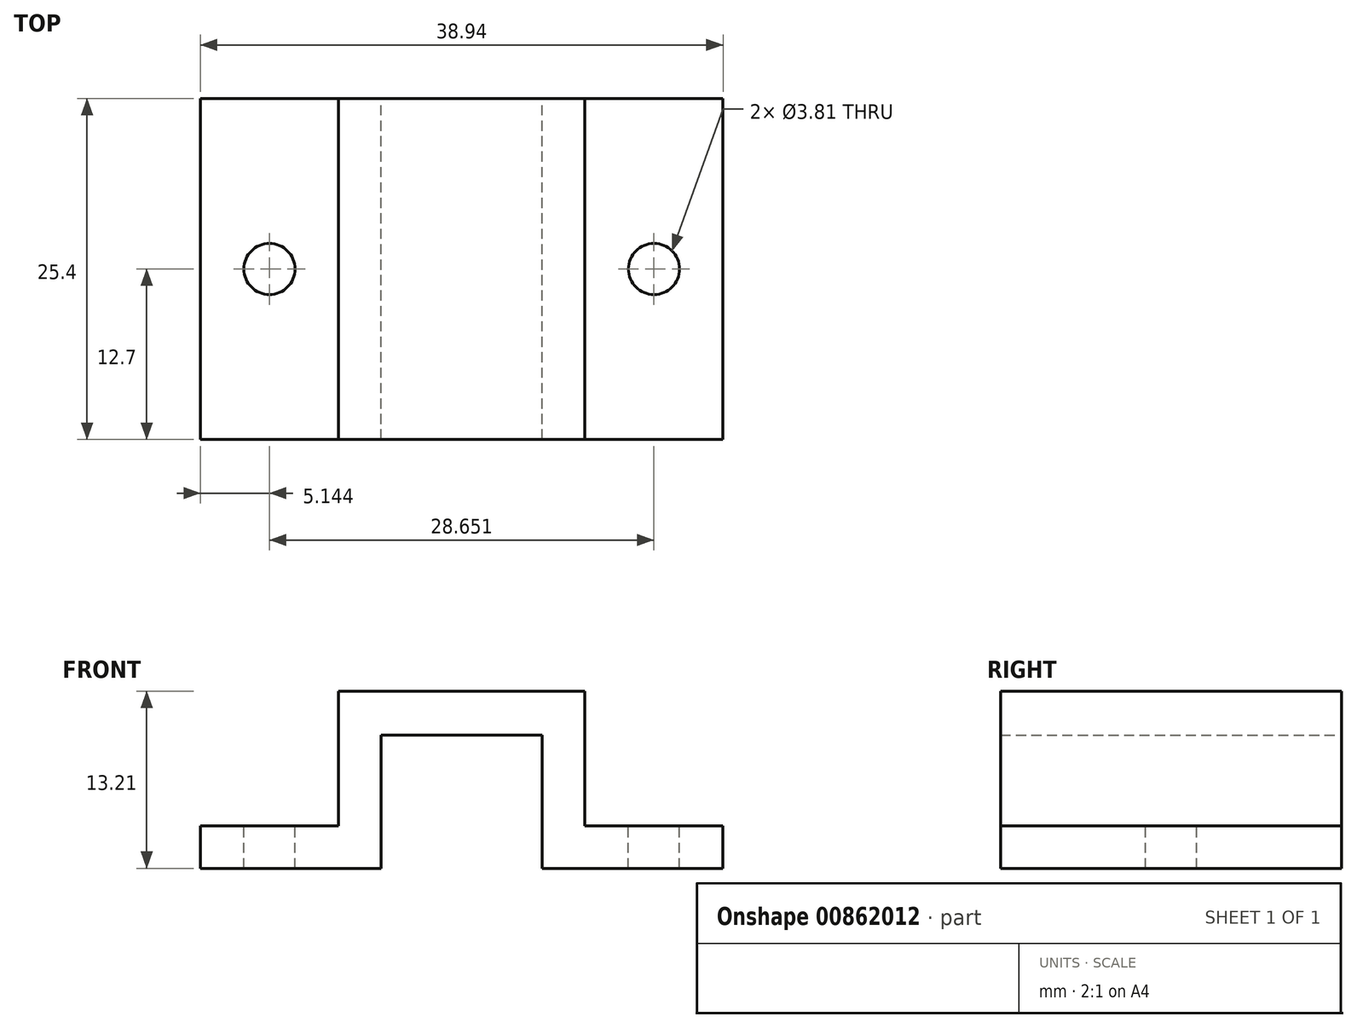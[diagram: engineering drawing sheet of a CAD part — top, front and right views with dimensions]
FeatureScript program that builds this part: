
annotation { "Feature Type Name" : "Feature", "Feature Type Description" : "" }
export const myFeature = defineFeature(function(context is Context, id is Id, definition is map)
    precondition{}
    {
        {
            var Q0;
            Q0=qCreatedBy(makeId("Front.planeOp"),FACE);
            var sketch = newSketch(context, id + "F0", { "sketchPlane" : qUnion([Q0])});
            skLineSegment(sketch, "E0", {"start": v(0, 0) * mm, "end": v(-6, 0) * mm});
            skLineSegment(sketch, "E1", {"start": v(-6, 0) * mm, "end": v(-6, -9.93) * mm});
            skLineSegment(sketch, "E2", {"start": v(-6, -9.93) * mm, "end": v(-19.47, -9.93) * mm});
            skLineSegment(sketch, "E3", {"start": v(-19.47, -9.93) * mm, "end": v(-19.47, -6.76) * mm});
            skLineSegment(sketch, "E4", {"start": v(-19.47, -6.76) * mm, "end": v(-9.18, -6.76) * mm});
            skLineSegment(sketch, "E5", {"start": v(-9.18, -6.76) * mm, "end": v(-9.18, 3.28) * mm});
            skLineSegment(sketch, "E6", {"start": v(-9.18, 3.28) * mm, "end": v(0, 3.28) * mm});
            skLineSegment(sketch, "E7.MirrorCS", {"start": v(6, 0) * mm, "end": v(6, -9.93) * mm});
            skLineSegment(sketch, "E8.MirrorCS", {"start": v(9.18, 3.28) * mm, "end": v(0, 3.28) * mm});
            skLineSegment(sketch, "E9.MirrorCS", {"start": v(9.18, -6.76) * mm, "end": v(9.18, 3.28) * mm});
            skLineSegment(sketch, "E10.MirrorCS", {"start": v(19.47, -9.93) * mm, "end": v(19.47, -6.76) * mm});
            skLineSegment(sketch, "E11.MirrorCS", {"start": v(19.47, -6.76) * mm, "end": v(9.18, -6.76) * mm});
            skLineSegment(sketch, "E12.MirrorCS", {"start": v(0, 0) * mm, "end": v(6, 0) * mm});
            skLineSegment(sketch, "E13.MirrorCS", {"start": v(6, -9.93) * mm, "end": v(19.47, -9.93) * mm});
            skSolve(sketch);
        }
        {
            var Q0;
            Q0=makeQuery(id+"F0.imprint","IMPRINT",FACE,{"disambiguationData":[TD([[makeQuery(id+"F0.imprint","IMPRINT",EDGE,{"derivedFrom":sQuery(id+"F0.wireOp",EDGE,"E0")}),-1.0]])]});
            extrude(context, id + "F1", {"entities" : qUnion([Q0]), "depth" : 25.4 * mm, "offsetDistance" : 25.4 * mm});
        }
        {
            var Q0;
            Q0=makeQuery(id+"F1.opExtrude","SWEPT_FACE",FACE,{"disambiguationData":[OSD([sQuery(id+"F0.wireOp",EDGE,"E4")])]});
            var sketch = newSketch(context, id + "F2", { "sketchPlane" : qUnion([Q0])});
            skLineSegment(sketch, "E14", {"start": v(-19.47, -12.7) * mm, "end": v(-9.18, -12.7) * mm, "construction": true});
            skLineSegment(sketch, "E15", {"start": v(-14.33, 0) * mm, "end": v(-14.33, -12.7) * mm, "construction": true});
            skCircle(sketch, "E16", {"center": v(-14.33, -12.7) * mm, "radius": 1.9 * mm});
            skCircle(sketch, "E17.MirrorC", {"center": v(14.33, -12.7) * mm, "radius": 1.9 * mm});
            skLineSegment(sketch, "E18.MirrorCS", {"start": v(14.33, 0) * mm, "end": v(14.33, -12.7) * mm, "construction": true});
            skLineSegment(sketch, "E19.MirrorCS", {"start": v(19.47, -12.7) * mm, "end": v(9.18, -12.7) * mm, "construction": true});
            skLineSegment(sketch, "E20", {"start": v(0, -12.7) * mm, "end": v(-14.33, -12.7) * mm, "construction": true});
            skSolve(sketch);
        }
        {
            var Q0;
            Q0 = qSketchRegion(id + "F2", true);
            extrude(context, id + "F3", {"entities" : qUnion([Q0]), "operationType" : NewBodyOperationType.REMOVE, "oppositeDirection" : true, "depth" : 25.4 * mm, "offsetDistance" : 25.4 * mm});
        }
    });
